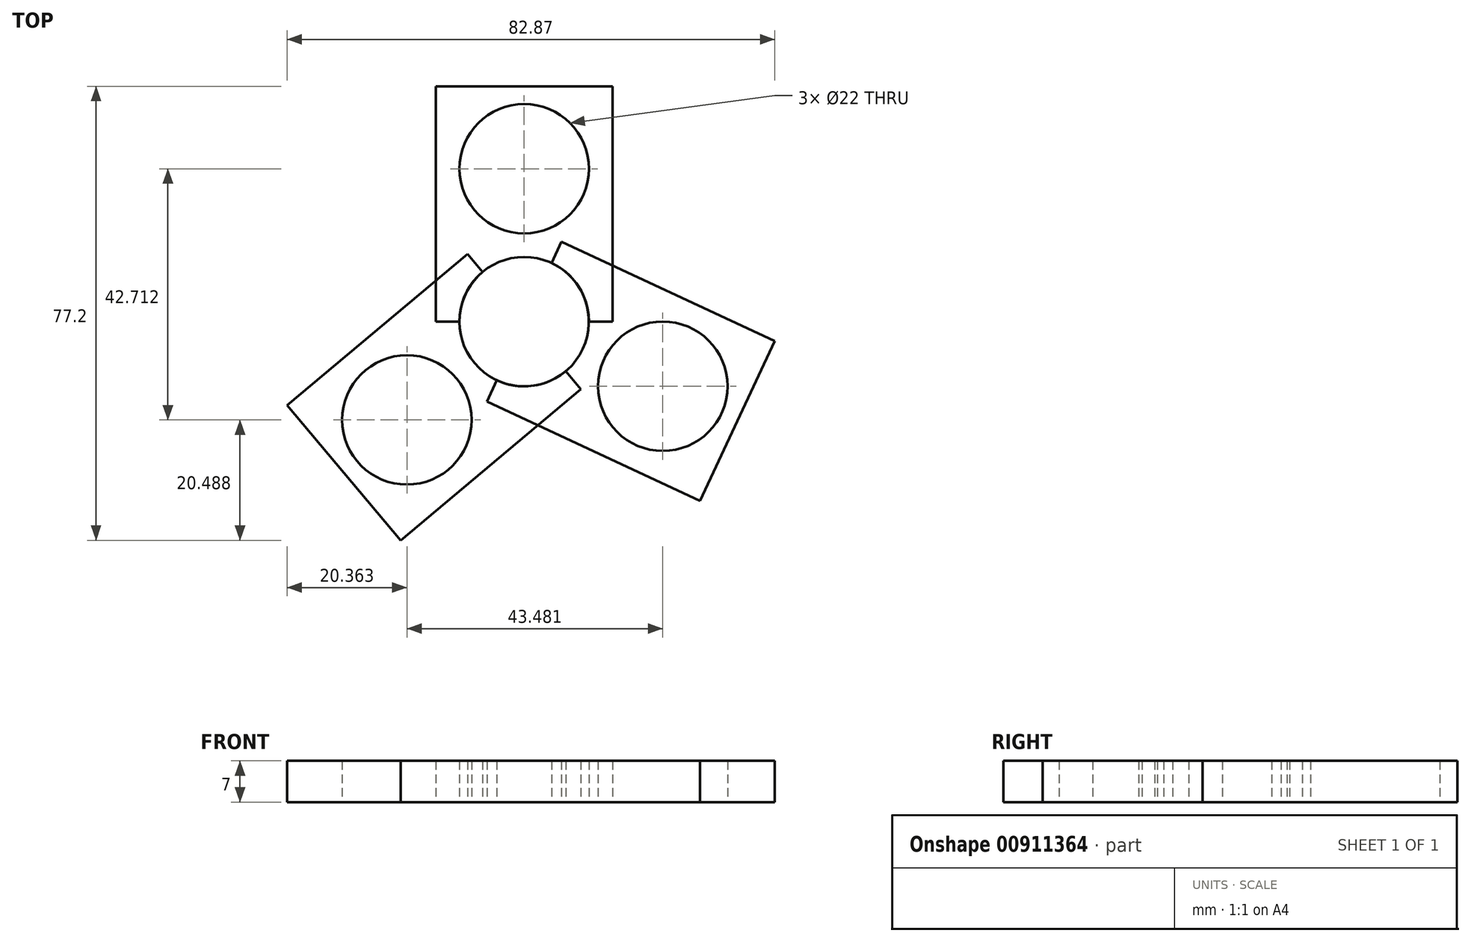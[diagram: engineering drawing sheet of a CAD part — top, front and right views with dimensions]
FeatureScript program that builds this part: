
annotation { "Feature Type Name" : "Feature", "Feature Type Description" : "" }
export const myFeature = defineFeature(function(context is Context, id is Id, definition is map)
    precondition{}
    {
        {
            var Q0;
            Q0=qCreatedBy(makeId("Top.planeOp"),FACE);
            var sketch = newSketch(context, id + "F0", { "sketchPlane" : qUnion([Q0])});
            skCircle(sketch, "E0", {"center": v(0, 0) * mm, "radius": 11 * mm});
            skLineSegment(sketch, "E1.bottom", {"start": v(0, 0) * mm, "end": v(15, 0) * mm});
            skLineSegment(sketch, "E1.top", {"start": v(0, 40) * mm, "end": v(15, 40) * mm});
            skLineSegment(sketch, "E1.left", {"start": v(0, 0) * mm, "end": v(0, 40) * mm});
            skLineSegment(sketch, "E1.right", {"start": v(15, 0) * mm, "end": v(15, 40) * mm});
            skLineSegment(sketch, "E2.bottom", {"start": v(0, 0) * mm, "end": v(-15, 0) * mm});
            skLineSegment(sketch, "E2.top", {"start": v(0, 40) * mm, "end": v(-15, 40) * mm});
            skLineSegment(sketch, "E2.right", {"start": v(-15, 0) * mm, "end": v(-15, 40) * mm});
            skLineSegment(sketch, "E3", {"start": v(0, 40) * mm, "end": v(0, 26) * mm});
            skCircle(sketch, "E4", {"center": v(0, 26) * mm, "radius": 11 * mm});
            skSolve(sketch);
        }
        {
            var Q0;
            {var subQ0=sQuery(id+"F0.wireOp",EDGE,"E2.top");Q0=makeQuery(id+"F0.imprint","IMPRINT",FACE,{"disambiguationData":[TD([[makeQuery(id+"F0.imprint","IMPRINT",EDGE,{"derivedFrom":subQ0}),1.0]])]});}
            var Q1;
            {var subQ9=sQuery(id+"F0.wireOp",EDGE,"E1.top");Q1=makeQuery(id+"F0.imprint","IMPRINT",FACE,{"disambiguationData":[TD([[makeQuery(id+"F0.imprint","IMPRINT",EDGE,{"derivedFrom":subQ9}),-1.0]])]});}
            extrude(context, id + "F1", {"entities" : qUnion([Q0, Q1]), "depth" : 7 * mm, "offsetDistance" : 25 * mm});
        }
        {
            var Q0;
            Q0=qCreatedBy(makeId("Front.planeOp"),FACE);
            var sketch = newSketch(context, id + "F2", { "sketchPlane" : qUnion([Q0])});
            skLineSegment(sketch, "E5", {"start": v(0, 0) * mm, "end": v(0, 34.91) * mm});
            skSolve(sketch);
        }
        {
            var Q0;
            Q0=makeQuery(id+"F1.opExtrude","SWEPT_BODY",BODY,{"disambiguationData":[OSD([sQuery(id+"F0.wireOp",EDGE,"E0"),sQuery(id+"F0.wireOp",EDGE,"E1.bottom"),sQuery(id+"F0.wireOp",EDGE,"E1.top"),sQuery(id+"F0.wireOp",EDGE,"E1.right"),sQuery(id+"F0.wireOp",EDGE,"E2.bottom"),sQuery(id+"F0.wireOp",EDGE,"E2.top"),sQuery(id+"F0.wireOp",EDGE,"E2.right"),sQuery(id+"F0.wireOp",EDGE,"E4")])]});
            var Q1;
            Q1=sQuery(id+"F2.wireOp",EDGE,"E5");
            transform(context, id + "F3", {"entities" : qUnion([Q0]), "transformType" : TransformType.ROTATION, "transformAxis" : qUnion([Q1]), "angle" : 130 * degree, "makeCopy" : true});
        }
        {
            var Q0;
            Q0=makeQuery(id+"F1.opExtrude","SWEPT_BODY",BODY,{"disambiguationData":[OSD([sQuery(id+"F0.wireOp",EDGE,"E0"),sQuery(id+"F0.wireOp",EDGE,"E1.bottom"),sQuery(id+"F0.wireOp",EDGE,"E1.top"),sQuery(id+"F0.wireOp",EDGE,"E1.right"),sQuery(id+"F0.wireOp",EDGE,"E2.bottom"),sQuery(id+"F0.wireOp",EDGE,"E2.top"),sQuery(id+"F0.wireOp",EDGE,"E2.right"),sQuery(id+"F0.wireOp",EDGE,"E4")])]});
            var Q1;
            Q1=sQuery(id+"F2.wireOp",EDGE,"E5");
            transform(context, id + "F4", {"entities" : qUnion([Q0]), "transformType" : TransformType.ROTATION, "transformAxis" : qUnion([Q1]), "angle" : 115 * degree, "oppositeDirection" : true, "makeCopy" : true});
        }
    });
